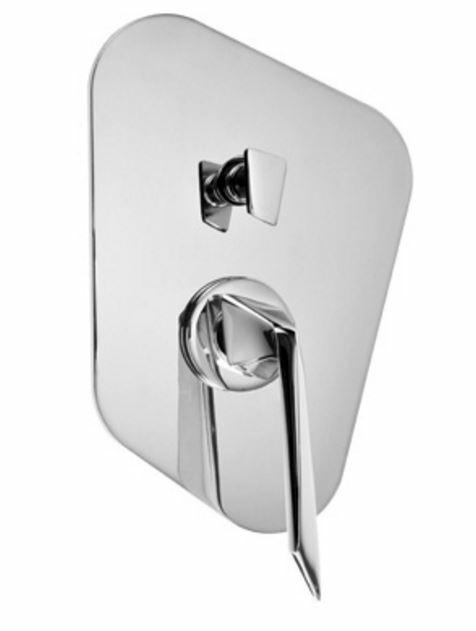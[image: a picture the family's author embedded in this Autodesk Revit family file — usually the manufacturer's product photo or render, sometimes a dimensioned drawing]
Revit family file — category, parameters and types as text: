
# Revit family: Monomando de Regadera PIU-201
name_source: partatom
category: Aparatos sanitarios
revit_build: Autodesk Revit 2016 (Build: 20150220_1215(x64)
units: mm (PartAtom-declared; Revit-internal decimal feet)

## family parameters
Compartido = Sí
Corte con vacíos al cargar = No
Cota de conector redondo = Diámetro de uso
Número OmniClass = 23.45.05.14.99
Punto de cálculo de habitación = Sí
Se basa en plano de trabajo = Sí
Siempre vertical = Sí
Tipo de pieza = Normal
Título OmniClass = Other Sanitary Washing Plumbing Fixtures

## types (1)
- PIU-201
    Brass Chromed = Brass
    Cartucho = Cartucho monomando cerámico  Ø40mm
    Comentarios de tipo = Monomando Piura
    Descripción = Monomando para Regadera sin Balanceo de Presión con Desviador
    Elevación por defecto = 1"
    Fabricante = HELVEX S.A. DE C.V.
    Garantía = El producto HELVEX está garantizado como libre de defectos en materiales y procesos de fabricación. El producto HELVEX está garantizado, en lo que se refiere a los acabados; por un periodo de 10 años en los acabados cromo y duravex, y por 2 años en cabados diferentes al cromo, a partir de la fecha de compra indicada en la factura.
    Imagen de tipo = PIU-201.JPG
    Instalación = ½" - 14 NPT
    Modelo = PIU-201
    Operación = Para abrir el flujo de agua levante la palanca maneral y gire para regular la temperatura.
    Presión máxima de trabajo = 85.3 psi
    Presión mínima de trabajo = 14.2 psi
    Support Base Diameter = 5"
    Total Height = 8"
    URL = http://www.helvex.com.mx

## geometry (parser evidence)
native form markers: Sweep x3
no freeform markers — native parametric forms only
